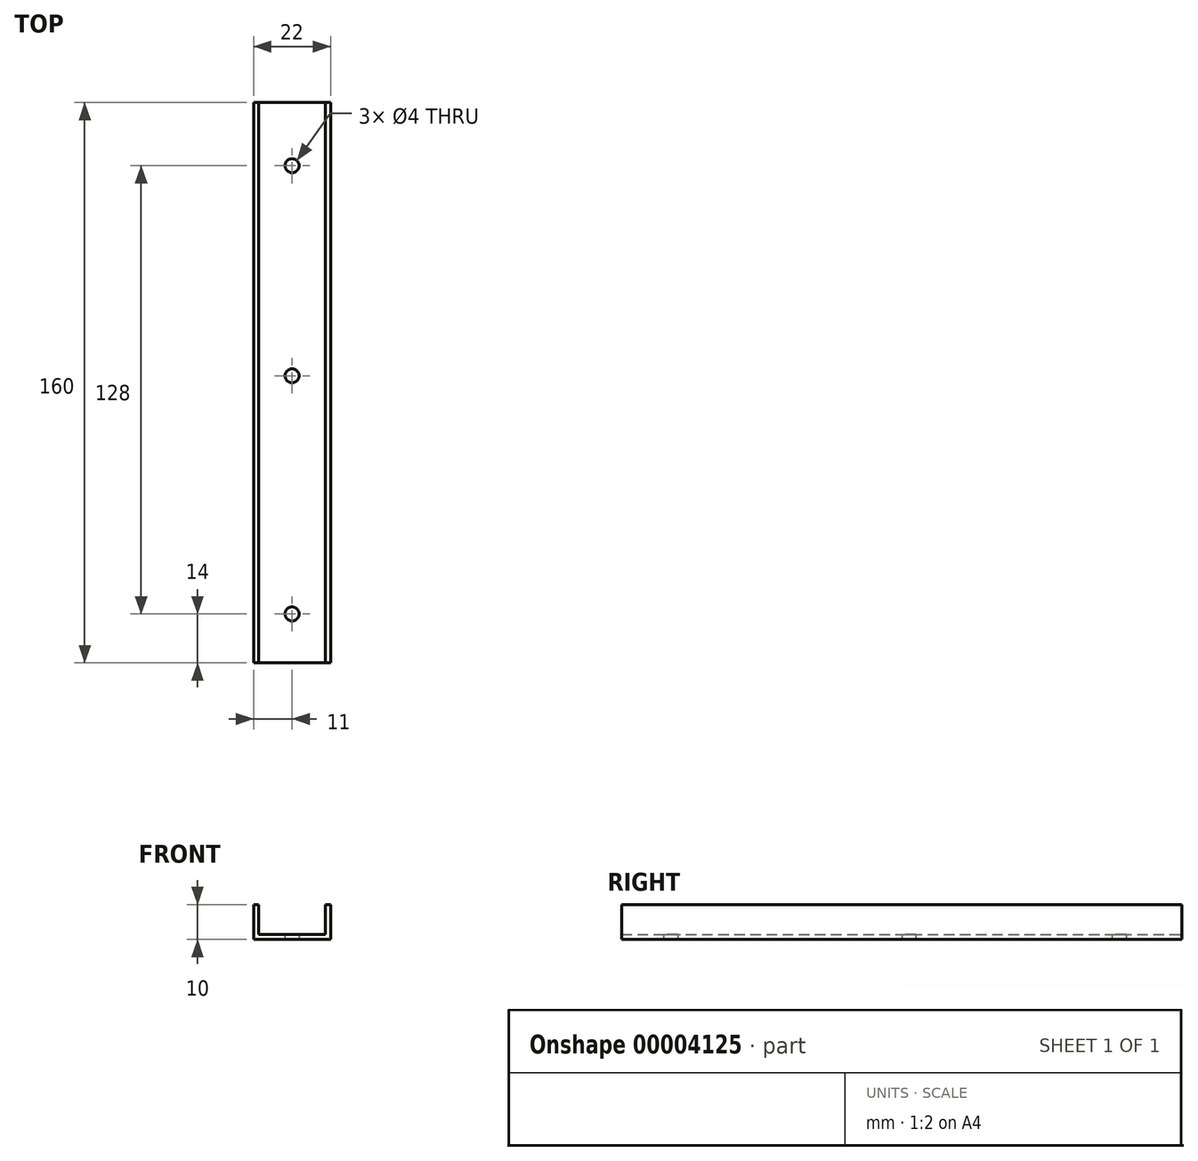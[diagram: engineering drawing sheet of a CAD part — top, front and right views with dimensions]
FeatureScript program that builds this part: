
annotation { "Feature Type Name" : "Feature", "Feature Type Description" : "" }
export const myFeature = defineFeature(function(context is Context, id is Id, definition is map)
    precondition{}
    {
        {
            var Q0;
            Q0=qCreatedBy(makeId("Front.planeOp"),FACE);
            var sketch = newSketch(context, id + "F0", { "sketchPlane" : qUnion([Q0])});
            skLineSegment(sketch, "E0", {"start": v(0, 0) * mm, "end": v(11, 0) * mm});
            skLineSegment(sketch, "E1", {"start": v(11, 0) * mm, "end": v(11, 10) * mm});
            skLineSegment(sketch, "E2", {"start": v(11, 10) * mm, "end": v(9.5, 10) * mm});
            skLineSegment(sketch, "E3", {"start": v(9.5, 10) * mm, "end": v(9.5, 1.5) * mm});
            skLineSegment(sketch, "E4", {"start": v(9.5, 1.5) * mm, "end": v(0, 1.5) * mm});
            skLineSegment(sketch, "E5.0.MirrorCS", {"start": v(-9.5, 1.5) * mm, "end": v(0, 1.5) * mm});
            skLineSegment(sketch, "E6.0.MirrorCS", {"start": v(0, 0) * mm, "end": v(-11, 0) * mm});
            skLineSegment(sketch, "E7.0.MirrorCS", {"start": v(-11, 0) * mm, "end": v(-11, 10) * mm});
            skLineSegment(sketch, "E8.0.MirrorCS", {"start": v(-11, 10) * mm, "end": v(-9.5, 10) * mm});
            skLineSegment(sketch, "E9.0.MirrorCS", {"start": v(-9.5, 10) * mm, "end": v(-9.5, 1.5) * mm});
            skSolve(sketch);
        }
        {
            var Q0;
            Q0=makeQuery(id+"F0.imprint","IMPRINT",FACE,{"disambiguationData":[TD([[makeQuery(id+"F0.imprint","IMPRINT",EDGE,{"derivedFrom":sQuery(id+"F0.wireOp",EDGE,"E1")}),1.0]])]});
            extrude(context, id + "F1", {"entities" : qUnion([Q0]), "depth" : 160 * mm});
        }
        {
            var Q0;
            Q0=makeQuery(id+"F1.opExtrude","SWEPT_FACE",FACE,{"disambiguationData":[OSD([sQuery(id+"F0.wireOp",EDGE,"E6.0.MirrorCS")])]});
            var sketch = newSketch(context, id + "F2", { "sketchPlane" : qUnion([Q0])});
            skLineSegment(sketch, "E10", {"start": v(0, 160) * mm, "end": v(0, 0) * mm});
            skCircle(sketch, "E11", {"center": v(0, 18) * mm, "radius": 2 * mm});
            skCircle(sketch, "E12", {"center": v(0, 78) * mm, "radius": 2 * mm});
            skCircle(sketch, "E13", {"center": v(0, 146) * mm, "radius": 2 * mm});
            skSolve(sketch);
        }
        {
            var Q0;
            {var subQ0=sQuery(id+"F2.wireOp",EDGE,"E12");var subQ1=sQuery(id+"F2.wireOp",EDGE,"E10");var subQ3=makeQuery(id+"F2.imprint","INTERSECT",VERTEX,{"disambiguationData":[OD(0.0)],"derivedFrom":[subQ1,subQ0]});Q0=makeQuery(id+"F2.imprint","IMPRINT",FACE,{"disambiguationData":[TD([[makeQuery(id+"F2.imprint","IMPRINT",EDGE,{"disambiguationData":[TD([[subQ3,-1.0]])],"derivedFrom":subQ1}),-1.0]])]});}
            var Q1;
            {var subQ0=sQuery(id+"F2.wireOp",EDGE,"E12");var subQ1=sQuery(id+"F2.wireOp",EDGE,"E10");var subQ3=makeQuery(id+"F2.imprint","INTERSECT",VERTEX,{"disambiguationData":[OD(0.0)],"derivedFrom":[subQ1,subQ0]});Q1=makeQuery(id+"F2.imprint","IMPRINT",FACE,{"disambiguationData":[TD([[makeQuery(id+"F2.imprint","IMPRINT",EDGE,{"disambiguationData":[TD([[subQ3,-1.0]])],"derivedFrom":subQ1}),1.0]])]});}
            var Q2;
            {var subQ0=sQuery(id+"F2.wireOp",EDGE,"E11");var subQ1=sQuery(id+"F2.wireOp",EDGE,"E10");var subQ3=makeQuery(id+"F2.imprint","INTERSECT",VERTEX,{"disambiguationData":[OD(0.0)],"derivedFrom":[subQ1,subQ0]});Q2=makeQuery(id+"F2.imprint","IMPRINT",FACE,{"disambiguationData":[TD([[makeQuery(id+"F2.imprint","IMPRINT",EDGE,{"disambiguationData":[TD([[subQ3,-1.0]])],"derivedFrom":subQ1}),-1.0]])]});}
            var Q3;
            {var subQ0=sQuery(id+"F2.wireOp",EDGE,"E11");var subQ1=sQuery(id+"F2.wireOp",EDGE,"E10");var subQ3=makeQuery(id+"F2.imprint","INTERSECT",VERTEX,{"disambiguationData":[OD(0.0)],"derivedFrom":[subQ1,subQ0]});Q3=makeQuery(id+"F2.imprint","IMPRINT",FACE,{"disambiguationData":[TD([[makeQuery(id+"F2.imprint","IMPRINT",EDGE,{"disambiguationData":[TD([[subQ3,-1.0]])],"derivedFrom":subQ1}),1.0]])]});}
            var Q4;
            {var subQ0=sQuery(id+"F2.wireOp",EDGE,"E13");var subQ1=sQuery(id+"F2.wireOp",EDGE,"E10");var subQ3=makeQuery(id+"F2.imprint","INTERSECT",VERTEX,{"disambiguationData":[OD(0.0)],"derivedFrom":[subQ1,subQ0]});Q4=makeQuery(id+"F2.imprint","IMPRINT",FACE,{"disambiguationData":[TD([[makeQuery(id+"F2.imprint","IMPRINT",EDGE,{"disambiguationData":[TD([[subQ3,-1.0]])],"derivedFrom":subQ1}),-1.0]])]});}
            var Q5;
            {var subQ0=sQuery(id+"F2.wireOp",EDGE,"E13");var subQ1=sQuery(id+"F2.wireOp",EDGE,"E10");var subQ3=makeQuery(id+"F2.imprint","INTERSECT",VERTEX,{"disambiguationData":[OD(0.0)],"derivedFrom":[subQ1,subQ0]});Q5=makeQuery(id+"F2.imprint","IMPRINT",FACE,{"disambiguationData":[TD([[makeQuery(id+"F2.imprint","IMPRINT",EDGE,{"disambiguationData":[TD([[subQ3,-1.0]])],"derivedFrom":subQ1}),1.0]])]});}
            extrude(context, id + "F3", {"entities" : qUnion([Q0, Q1, Q2, Q3, Q4, Q5]), "operationType" : NewBodyOperationType.REMOVE, "oppositeDirection" : true, "depth" : 25 * mm});
        }
    });
